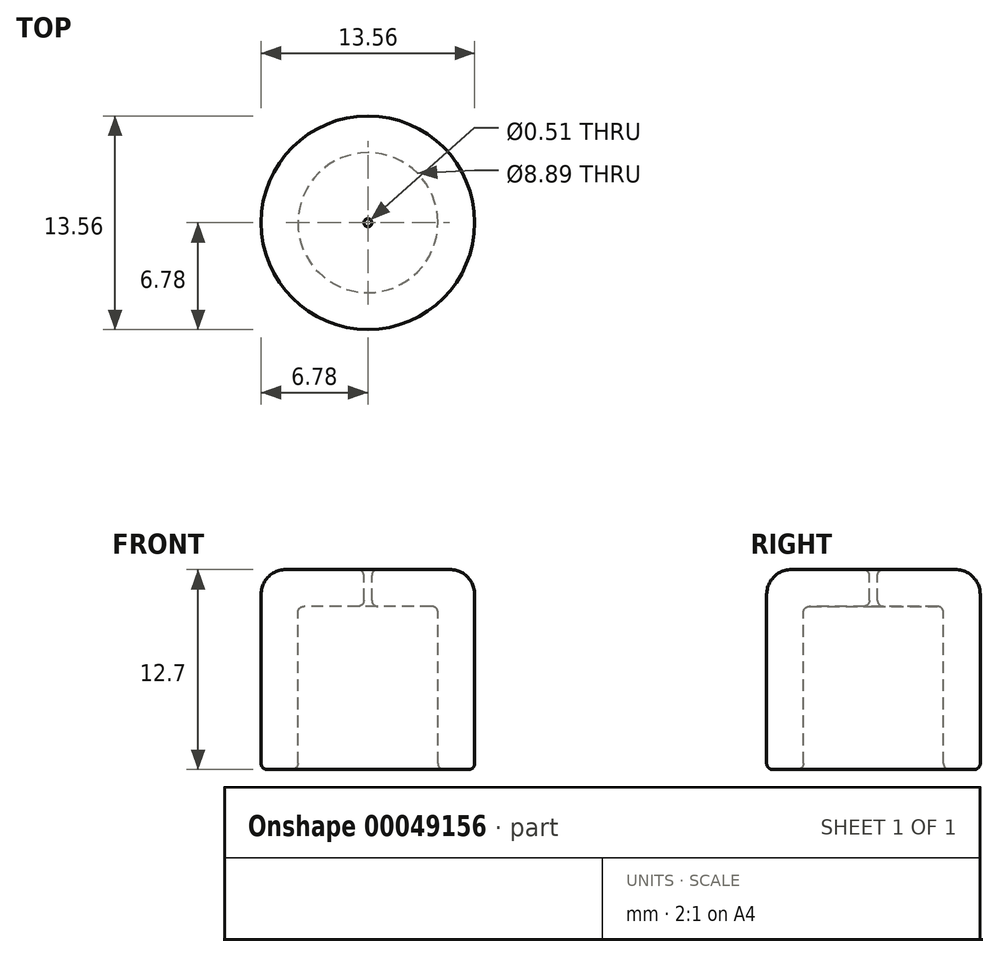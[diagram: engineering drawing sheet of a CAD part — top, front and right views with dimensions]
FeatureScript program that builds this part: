
annotation { "Feature Type Name" : "Feature", "Feature Type Description" : "" }
export const myFeature = defineFeature(function(context is Context, id is Id, definition is map)
    precondition{}
    {
        {
            var Q0;
            Q0=qCreatedBy(makeId("Right.planeOp"),FACE);
            var sketch = newSketch(context, id + "F0", { "sketchPlane" : qUnion([Q0])});
            skLineSegment(sketch, "E0", {"start": v(0, 18.98) * mm, "end": v(0, 0) * mm, "construction": true});
            skLineSegment(sketch, "E1", {"start": v(4.83, 0) * mm, "end": v(6.4, 0) * mm});
            skLineSegment(sketch, "E2", {"start": v(6.78, 0.38) * mm, "end": v(6.78, 11.13) * mm});
            skLineSegment(sketch, "E3", {"start": v(4.44, 9.98) * mm, "end": v(4.45, 0.38) * mm});
            skPoint(sketch, "E4.visualSharp", {"position": v(6.78, 8.76) * mm});
            skLineSegment(sketch, "E5", {"start": v(0.63, 12.7) * mm, "end": v(5.2, 12.7) * mm});
            skLineSegment(sketch, "E6", {"start": v(0.25, 12.32) * mm, "end": v(0.25, 10.74) * mm});
            skLineSegment(sketch, "E7", {"start": v(0.63, 10.36) * mm, "end": v(4.06, 10.36) * mm});
            skPoint(sketch, "E8.visualSharp", {"position": v(6.78, 12.7) * mm});
            skArc(sketch, "E8.filletArc", {"start": v(6.78, 11.13) * mm, "mid": v(6.32, 12.24) * mm, "end": v(5.2, 12.7) * mm});
            skPoint(sketch, "E9.visualSharp", {"position": v(4.45, 0) * mm});
            skArc(sketch, "E9.filletArc", {"start": v(4.45, 0.38) * mm, "mid": v(4.56, 0.11) * mm, "end": v(4.83, 0) * mm});
            skPoint(sketch, "E10.visualSharp", {"position": v(6.78, 0) * mm});
            skArc(sketch, "E10.filletArc", {"start": v(6.4, 0) * mm, "mid": v(6.67, 0.11) * mm, "end": v(6.78, 0.38) * mm});
            skPoint(sketch, "E11.visualSharp", {"position": v(0.25, 12.7) * mm});
            skArc(sketch, "E11.filletArc", {"start": v(0.63, 12.7) * mm, "mid": v(0.37, 12.59) * mm, "end": v(0.25, 12.32) * mm});
            skPoint(sketch, "E12.visualSharp", {"position": v(4.44, 10.36) * mm});
            skArc(sketch, "E12.filletArc", {"start": v(4.44, 9.98) * mm, "mid": v(4.33, 10.25) * mm, "end": v(4.06, 10.36) * mm});
            skPoint(sketch, "E13.visualSharp", {"position": v(0.25, 10.36) * mm});
            skArc(sketch, "E13.filletArc", {"start": v(0.25, 10.74) * mm, "mid": v(0.37, 10.47) * mm, "end": v(0.63, 10.36) * mm});
            skSolve(sketch);
        }
        {
            var Q0;
            Q0=makeQuery(id+"F0.imprint","IMPRINT",FACE,{"disambiguationData":[TD([[makeQuery(id+"F0.imprint","IMPRINT",EDGE,{"derivedFrom":sQuery(id+"F0.wireOp",EDGE,"E1")}),1.0]])]});
            var Q1;
            Q1=sQuery(id+"F0.wireOp",EDGE,"E0");
            revolve(context, id + "F1", {"entities" : qUnion([Q0]), "axis" : qUnion([Q1]), "revolveType" : RevolveType.FULL});
        }
    });
